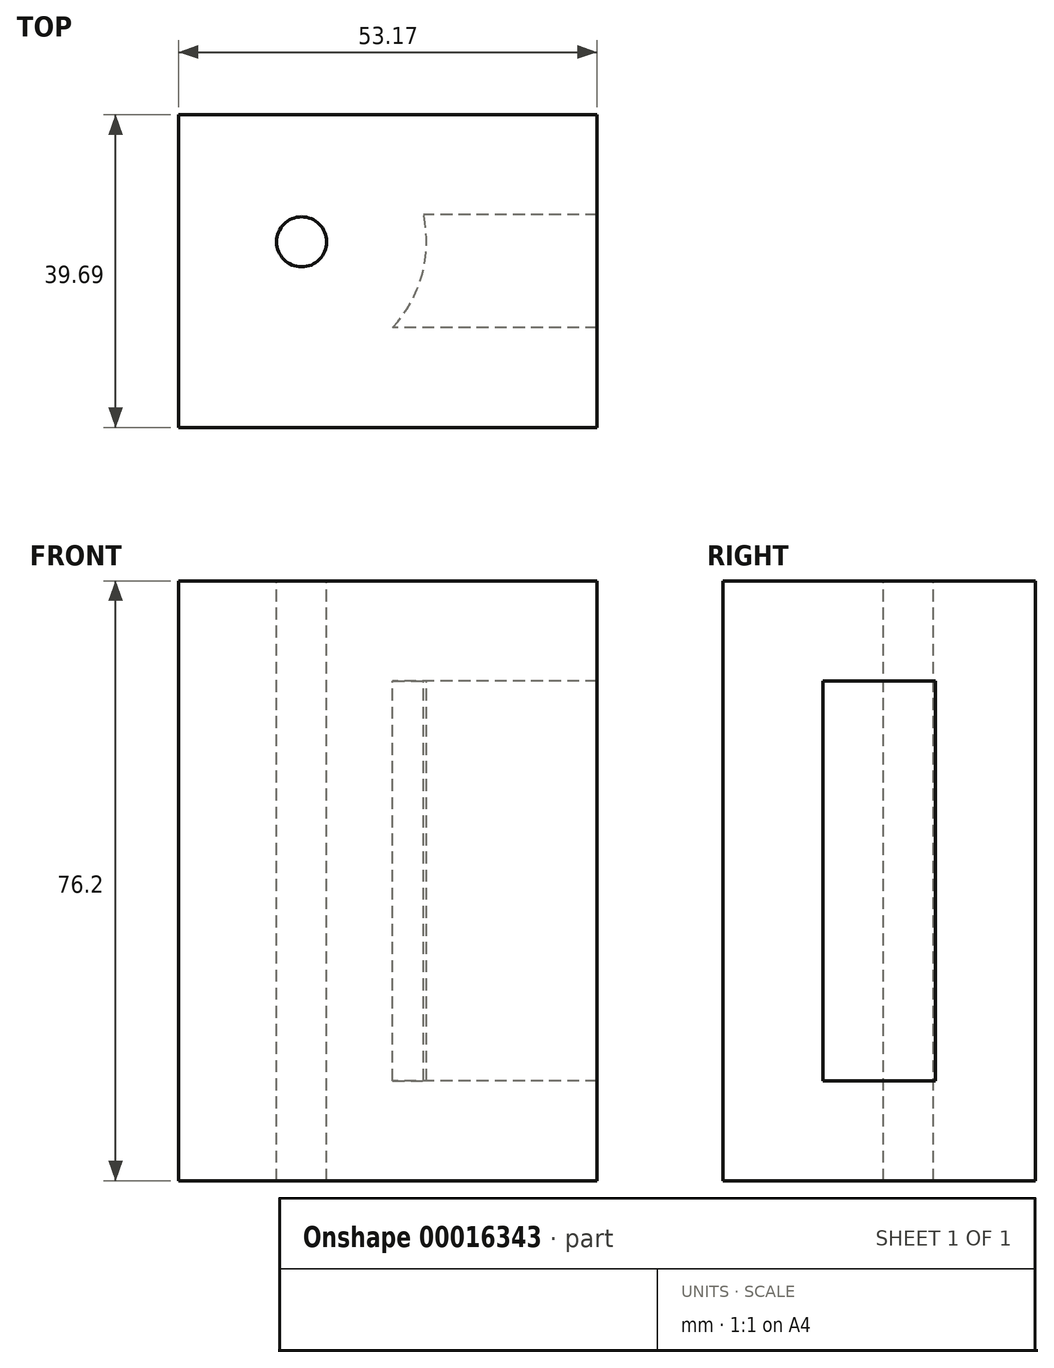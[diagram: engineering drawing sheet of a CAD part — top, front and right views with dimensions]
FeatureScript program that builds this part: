
annotation { "Feature Type Name" : "Feature", "Feature Type Description" : "" }
export const myFeature = defineFeature(function(context is Context, id is Id, definition is map)
    precondition{}
    {
        {
            var Q0;
            Q0=qCreatedBy(makeId("Top.planeOp"),FACE);
            var sketch = newSketch(context, id + "F0", { "sketchPlane" : qUnion([Q0])});
            skLineSegment(sketch, "E0.bottom", {"start": v(0, 0) * mm, "end": v(-53.17, 0) * mm});
            skLineSegment(sketch, "E0.top", {"start": v(0, 39.69) * mm, "end": v(-53.17, 39.69) * mm});
            skLineSegment(sketch, "E0.left", {"start": v(0, 0) * mm, "end": v(0, 39.69) * mm});
            skLineSegment(sketch, "E0.right", {"start": v(-53.17, 0) * mm, "end": v(-53.17, 39.69) * mm});
            skSolve(sketch);
        }
        {
            var Q0;
            Q0=makeQuery(id+"F0.imprint","IMPRINT",FACE,{"disambiguationData":[TD([[makeQuery(id+"F0.imprint","IMPRINT",EDGE,{"derivedFrom":sQuery(id+"F0.wireOp",EDGE,"E0.bottom")}),-1.0]])]});
            extrude(context, id + "F1", {"entities" : qUnion([Q0]), "depth" : 76.2 * mm});
        }
        {
            var Q0;
            Q0=makeQuery(id+"F1.opExtrude","CAP_FACE",FACE,{"disambiguationData":[OSD([sQuery(id+"F0.wireOp",EDGE,"E0.bottom"),sQuery(id+"F0.wireOp",EDGE,"E0.top"),sQuery(id+"F0.wireOp",EDGE,"E0.left"),sQuery(id+"F0.wireOp",EDGE,"E0.right")])],"isStart":false});
            var sketch = newSketch(context, id + "F2", { "sketchPlane" : qUnion([Q0])});
            skCircle(sketch, "E1", {"center": v(-37.55, 23.56) * mm, "radius": 7.36 * mm});
            skSolve(sketch);
        }
        {
            var Q0;
            Q0=sQuery(id+"F2.wireOp",VERTEX,"E1.center");
            var Q1;
            Q1=makeQuery(id+"F1.opExtrude","SWEPT_BODY",BODY,{"disambiguationData":[OSD([sQuery(id+"F0.wireOp",EDGE,"E0.bottom"),sQuery(id+"F0.wireOp",EDGE,"E0.top"),sQuery(id+"F0.wireOp",EDGE,"E0.left"),sQuery(id+"F0.wireOp",EDGE,"E0.right")])]});
            hole(context, id + "F3", {"style" : HoleStyle.SIMPLE, "holeDiameter" : 6.35 * mm, "endStyle" : HoleEndStyle.THROUGH, "locations" : qUnion([Q0]), "scope" : qUnion([Q1])});
        }
        {
            var Q0;
            Q0=makeQuery(id+"F1.opExtrude","SWEPT_FACE",FACE,{"disambiguationData":[OSD([sQuery(id+"F0.wireOp",EDGE,"E0.left")])]});
            shell(context, id + "F4", {"entities" : qUnion([Q0]), "thickness" : 12.7 * mm});
        }
    });
